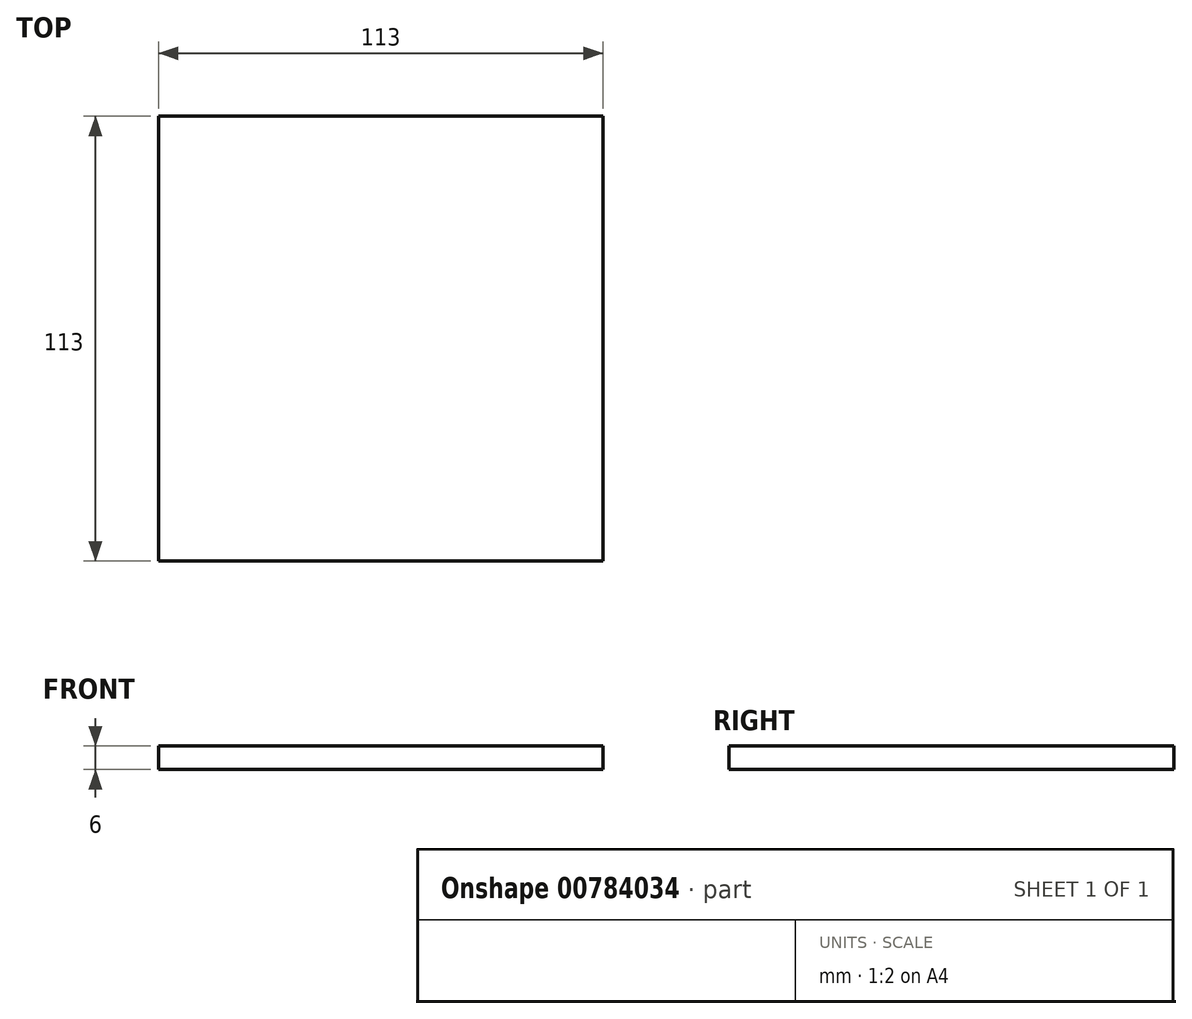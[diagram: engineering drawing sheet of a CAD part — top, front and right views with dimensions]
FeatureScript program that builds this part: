
annotation { "Feature Type Name" : "Feature", "Feature Type Description" : "" }
export const myFeature = defineFeature(function(context is Context, id is Id, definition is map)
    precondition{}
    {
        {
            var Q0;
            Q0=qCreatedBy(makeId("Top.planeOp"),FACE);
            var sketch = newSketch(context, id + "F0", { "sketchPlane" : qUnion([Q0])});
            skLineSegment(sketch, "E0.bottom", {"start": v(56.5, -56.5) * mm, "end": v(-56.5, -56.5) * mm});
            skLineSegment(sketch, "E0.top", {"start": v(56.5, 56.5) * mm, "end": v(-56.5, 56.5) * mm});
            skLineSegment(sketch, "E0.left", {"start": v(56.5, -56.5) * mm, "end": v(56.5, 56.5) * mm});
            skLineSegment(sketch, "E0.right", {"start": v(-56.5, -56.5) * mm, "end": v(-56.5, 56.5) * mm});
            skPoint(sketch, "E0.middle", {"position": v(0, 0) * mm});
            skSolve(sketch);
        }
        {
            var Q0;
            Q0=makeQuery(id+"F0.imprint","IMPRINT",FACE,{"disambiguationData":[TD([[makeQuery(id+"F0.imprint","IMPRINT",EDGE,{"derivedFrom":sQuery(id+"F0.wireOp",EDGE,"E0.bottom")}),-1.0]])]});
            extrude(context, id + "F1", {"entities" : qUnion([Q0]), "depth" : 6 * mm, "offsetDistance" : 25 * mm});
        }
    });
